# Revit family: 90000359 - Aventa Silent AVS125 - BIM file
name_source: partatom
category: Mechanical Equipment
units: mm (PartAtom-declared; Revit-internal decimal feet)

## family parameters
Always vertical = No
Classification = None
Cut with Voids When Loaded = No
Maintain Annotation Orientation = No
OmniClass Number = 23.75.35.17.11
OmniClass Title = Fans for Air Ductwork
Part Type = Breaks Into
Room Calculation Point = No
Round Connector Dimension = Use Diameter
Shared = No
Work Plane-Based = No

## types (2) — shared parameters
Current = 0 A
D = 125 mm  [stored 0.410105 ft]
D1 = 214 mm  [stored 0.7021 ft]
Dd12 = 3 mm  [stored 0.00984252 ft]
Dd13 = 4 mm  [stored 0.0131234 ft]
Dd14 = 28 mm  [stored 0.0918635 ft]
Dd16 = 41 mm  [stored 0.134514 ft]
Dd22 = 3 mm  [stored 0.00984252 ft]
Dd23 = 4 mm  [stored 0.0131234 ft]
Dd24 = 26 mm
Dd26 = 41 mm  [stored 0.134514 ft]
Description = Inline mixed-flow fan suitable for domestic and light commercial facilities
Dimensions = (H) 237 x (W) 474 x (D) 243mm
Distribution Box Material = Distribution Box Dark Grey
Duct Connection Size = 125 mm  [stored 0.410105 ft]
ElBoxH = 124 mm  [stored 0.406824 ft]
ElBoxL = 98 mm  [stored 0.321522 ft]
ElBoxR = 15 mm  [stored 0.0492126 ft]
ElBoxW = 116 mm  [stored 0.380577 ft]
Family Version = 1.0
Fan Material = Metal Black
Hanger Material = Metal Zinc
HangerBaseH = 113 mm  [stored 0.370735 ft]
HangerExtraL = Yes
HangerH = 113 mm  [stored 0.370735 ft]
HangerL = 208 mm
HangerL1 = 208 mm
HangerW = 93 mm  [stored 0.305118 ft]
L = 474 mm  [stored 1.55512 ft]
L1 = 25 mm  [stored 0.082021 ft]
L11 = 123 mm  [stored 0.403543 ft]
L12 = 8 mm  [stored 0.0262467 ft]
L13 = 13 mm
L14 = 19 mm  [stored 0.062336 ft]
L15 = 69 mm
L16 = 8 mm  [stored 0.0262467 ft]
L17 = 6 mm  [stored 0.019685 ft]
L2 = 25 mm  [stored 0.082021 ft]
L21 = 169 mm  [stored 0.554462 ft]
L22 = 8 mm  [stored 0.0262467 ft]
L23 = 13 mm
L24 = 24 mm  [stored 0.0787402 ft]
L25 = 110 mm
L26 = 8 mm  [stored 0.0262467 ft]
L27 = 6 mm  [stored 0.019685 ft]
Load Classification = HVAC
Maintenance Zone Height = 600 mm  [stored 1.9685 ft]
Maintenance Zone Length = 600 mm  [stored 1.9685 ft]
Maintenance Zone Length Calc = 600 mm  [stored 1.9685 ft]
Maintenance Zone Material = Maintenance Zone
Maintenance Zone Width = 600 mm  [stored 1.9685 ft]
Manufacturer = Airflow
Material Finish = Polymer Coated Steel
Number of Poles = 1
Power Factor = 1
Protection rating = IPX4
R1 = 107 mm  [stored 0.35105 ft]
RPM (min-1) = 2310
Transported Air Temperature (°C) = -25...+60
URL = https://www.airflow.com
Voltage = 230 V
Weight = 4.60 kg
zero-valued in all types: Default Elevation

## per-type parameters (varying)
| type | Airflow part no | Apparent Power | Maximum Air Flow | Noise Level at 3 m (dBa) | Power | Type Comments |
| Aventa Silent AVS125 Timer | 90002119 | 30 VA | 340 m³/h | 28 | 30 W | Inline fan single speed up to 340m3/h |
| Aventa Silent AVS125 Basic | 90000359 | 25 VA | 230 m³/h | 23 | 25 W | Inline fan single speed up to 230m3/h |

note: column(s) folded — value = type name in every type: Model

note: [stored X ft] marks values corroborated as IEEE doubles in the binary element streams (Revit-internal decimal feet)

## geometry (parser evidence)
native form markers: Sweep x9
no freeform markers — native parametric forms only
